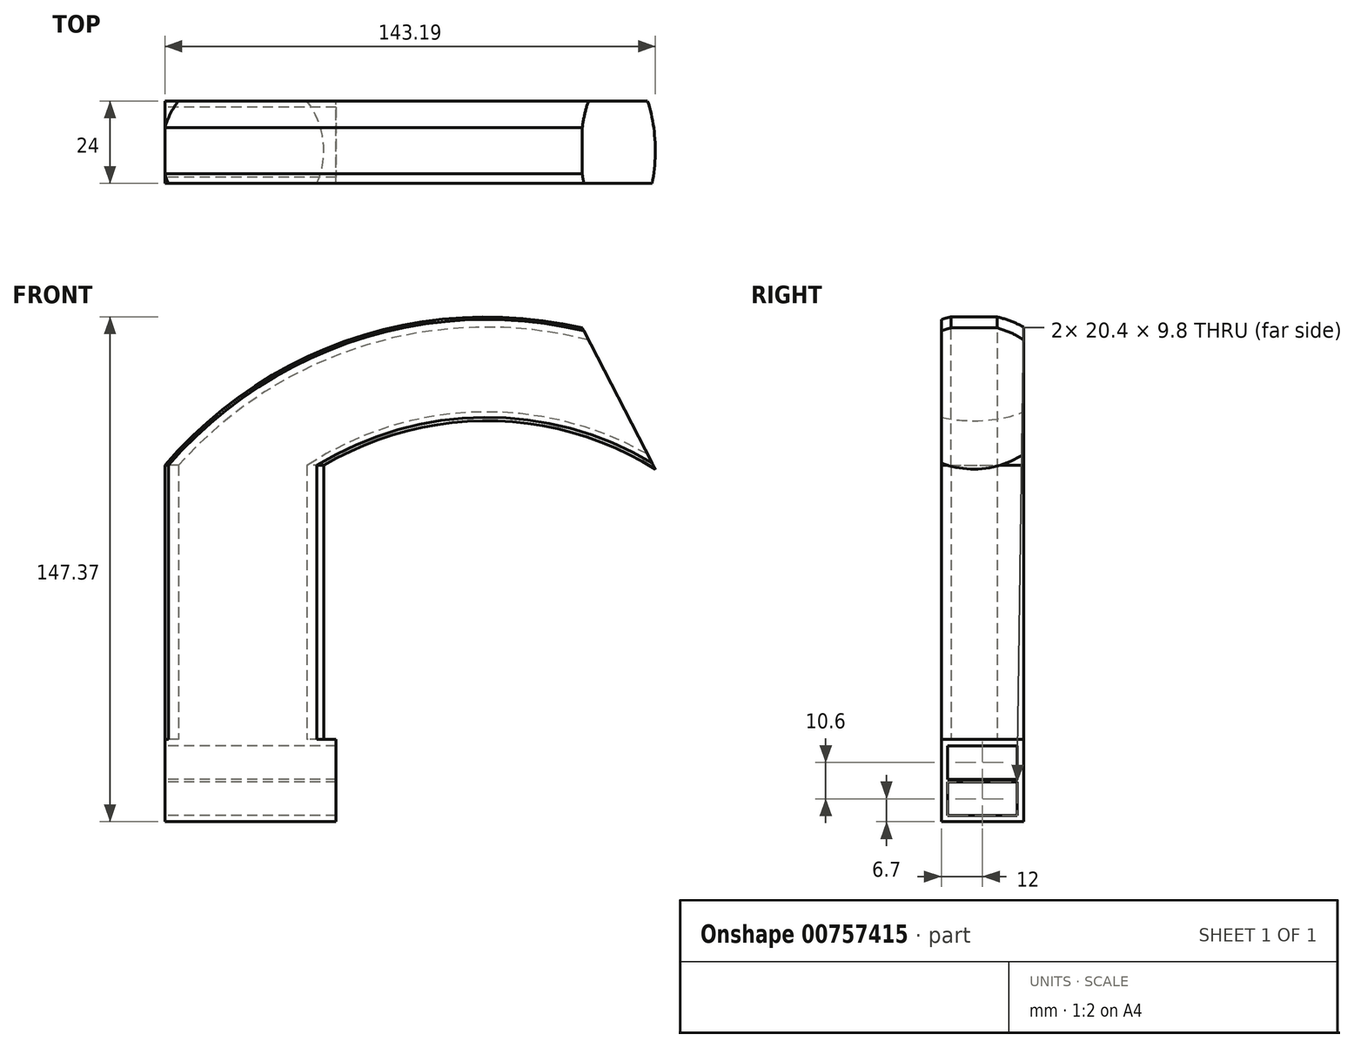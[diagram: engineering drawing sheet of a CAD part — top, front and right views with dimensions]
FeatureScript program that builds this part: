
annotation { "Feature Type Name" : "Feature", "Feature Type Description" : "" }
export const myFeature = defineFeature(function(context is Context, id is Id, definition is map)
    precondition{}
    {
        {
            var Q0;
            Q0=qCreatedBy(makeId("Front.planeOp"),FACE);
            var sketch = newSketch(context, id + "F0", { "sketchPlane" : qUnion([Q0])});
            skLineSegment(sketch, "E0.bottom", {"start": v(-43.92, 0) * mm, "end": v(-93.92, 0) * mm});
            skLineSegment(sketch, "E0.top", {"start": v(-43.92, 24) * mm, "end": v(-93.92, 24) * mm});
            skLineSegment(sketch, "E0.left", {"start": v(-43.92, 0) * mm, "end": v(-43.92, 24) * mm});
            skLineSegment(sketch, "E0.right", {"start": v(-93.92, 0) * mm, "end": v(-93.92, 24) * mm});
            skSolve(sketch);
        }
        {
            var Q0;
            Q0 = qSketchRegion(id + "F0", true);
            extrude(context, id + "F1", {"entities" : qUnion([Q0]), "depth" : 24 * mm, "offsetDistance" : 25 * mm});
        }
        {
            var Q0;
            Q0=makeQuery(id+"F1.opExtrude","SWEPT_FACE",FACE,{"disambiguationData":[OSD([sQuery(id+"F0.wireOp",EDGE,"E0.top")])]});
            var sketch = newSketch(context, id + "F2", { "sketchPlane" : qUnion([Q0])});
            skCircle(sketch, "E1", {"center": v(-71.2, -14.47) * mm, "radius": 23.7 * mm});
            skLineSegment(sketch, "E2", {"start": v(0, 70.34) * mm, "end": v(0, -64.39) * mm, "construction": true});
            skSolve(sketch);
        }
        {
            var Q0;
            Q0=makeQuery(id+"F1.opExtrude","SWEPT_FACE",FACE,{"disambiguationData":[OSD([sQuery(id+"F0.wireOp",EDGE,"E0.right")])]});
            var sketch = newSketch(context, id + "F3", { "sketchPlane" : qUnion([Q0])});
            skLineSegment(sketch, "E3.bottom", {"start": v(1.8, 1.8) * mm, "end": v(22.2, 1.8) * mm});
            skLineSegment(sketch, "E3.top", {"start": v(1.8, 22.2) * mm, "end": v(22.2, 22.2) * mm});
            skLineSegment(sketch, "E3.left", {"start": v(1.8, 1.8) * mm, "end": v(1.8, 22.2) * mm});
            skLineSegment(sketch, "E3.right", {"start": v(22.2, 1.8) * mm, "end": v(22.2, 22.2) * mm});
            skLineSegment(sketch, "E4", {"start": v(12, 0) * mm, "end": v(12, 1.8) * mm, "construction": true});
            skLineSegment(sketch, "E5", {"start": v(0, 12) * mm, "end": v(22.2, 12) * mm, "construction": true});
            skLineSegment(sketch, "E6.bottom", {"start": v(1.8, 12.4) * mm, "end": v(22.2, 12.4) * mm});
            skLineSegment(sketch, "E6.top", {"start": v(1.8, 11.6) * mm, "end": v(22.2, 11.6) * mm});
            skLineSegment(sketch, "E6.left", {"start": v(1.8, 12.4) * mm, "end": v(1.8, 11.6) * mm});
            skLineSegment(sketch, "E6.right", {"start": v(22.2, 12.4) * mm, "end": v(22.2, 11.6) * mm});
            skSolve(sketch);
        }
        {
            var Q0;
            Q0=makeQuery(id+"F3.imprint","IMPRINT",FACE,{"disambiguationData":[TD([[makeQuery(id+"F3.imprint","IMPRINT",EDGE,{"derivedFrom":sQuery(id+"F3.wireOp",EDGE,"E3.bottom")}),1.0]])]});
            var Q1;
            {var subQ0=sQuery(id+"F3.wireOp",EDGE,"E3.top");Q1=makeQuery(id+"F3.imprint","IMPRINT",FACE,{"disambiguationData":[TD([[makeQuery(id+"F3.imprint","IMPRINT",EDGE,{"derivedFrom":subQ0}),-1.0]])]});}
            extrude(context, id + "F4", {"entities" : qUnion([Q0, Q1]), "operationType" : NewBodyOperationType.REMOVE, "endBound" : BoundingType.THROUGH_ALL, "oppositeDirection" : true, "depth" : 25 * mm, "offsetDistance" : 25 * mm});
        }
        {
            var Q0;
            {var subQ0=sQuery(id+"F2.wireOp",EDGE,"E1");var subQ1=sQuery(id+"F0.wireOp",EDGE,"E0.top");var subQ5=makeQuery(id+"F1.opExtrude","CAP_EDGE",EDGE,{"disambiguationData":[OSD([subQ1])],"isStart":true});var subQ6=makeQuery(id+"F2.imprint","INTERSECT",VERTEX,{"disambiguationData":[OD(1.0)],"derivedFrom":[subQ5,subQ0]});Q0=makeQuery(id+"F2.imprint","IMPRINT",FACE,{"disambiguationData":[TD([[makeQuery(id+"F2.imprint","IMPRINT",EDGE,{"disambiguationData":[TD([[subQ6,1.0]])],"derivedFrom":subQ0}),1.0]])]});}
            extrude(context, id + "F5", {"entities" : qUnion([Q0]), "operationType" : NewBodyOperationType.ADD, "depth" : 80 * mm, "offsetDistance" : 25 * mm});
        }
        {
            var Q0;
            Q0=makeQuery(id+"F5.opExtrude","CAP_FACE",FACE,{"disambiguationData":[OSD([sQuery(id+"F0.wireOp",EDGE,"E0.top"),sQuery(id+"F0.wireOp",EDGE,"E0.right"),sQuery(id+"F2.wireOp",EDGE,"E1")])],"isStart":false});
            var sketch = newSketch(context, id + "F6", { "sketchPlane" : qUnion([Q0])});
            skCircle(sketch, "E7", {"center": v(-71.2, -14.47) * mm, "radius": 23.7 * mm});
            skSolve(sketch);
        }
        {
            var Q0;
            {var subQ2=sQuery(id+"F0.wireOp",EDGE,"E0.top");var subQ7=makeQuery(id+"F5.opExtrude","CAP_EDGE",EDGE,{"disambiguationData":[OSD([subQ2,sQuery(id+"F0.wireOp",EDGE,"E0.right")])],"isStart":false});Q0=makeQuery(id+"F6.imprint","IMPRINT",FACE,{"disambiguationData":[TD([[makeQuery(id+"F6.imprint","IMPRINT",EDGE,{"derivedFrom":subQ7}),-1.0]])]});}
            var Q1;
            Q1=sQuery(id+"F2.wireOp",EDGE,"E2");
            revolve(context, id + "F7", {"operationType" : NewBodyOperationType.ADD, "surfaceOperationType" : NewSurfaceOperationType.NEW, "entities" : qUnion([Q0]), "axis" : qUnion([Q1]), "revolveType" : RevolveType.ONE_DIRECTION, "oppositeDirection" : true, "angle" : 62.67 * degree});
        }
    });
